# Revit family: efg_egg-20_60s(t)b2_60Hz
name_source: partatom
category: 機械設備
units: mm (PartAtom-declared; Revit-internal decimal feet)

## family parameters
OmniClass タイトル = Industrial Ventilating Equipment
OmniClass 番号 = 23.75.35.21.17
パーツ タイプ = 標準
ロード時にボイドで切り取り = はい
丸型コネクタ寸法 = 直径を使用
作業面ベース = いいえ
共有 = いいえ
常に垂直 = はい
部屋計算ポイント = いいえ

## types (8) — shared parameters
IfcExportAs = IfcFanType
IfcExportType = TUBEAXIAL
MID風量 = 0.0 m³/h
OmniClassCode = 23-33 31 19 11 17
URL = https://www.mitsubishielectric.co.jp
Uniclass2015Code = Pr_65_67_29_67
Uniclass2015Title = Propeller fans
Uniclass2015Version = Systems v1.9
ファンの種類 = 軸流羽根
仕様書バージョン = Version1.0
企業コード = 108420
分類コード = 50052503100110
周波数 = 60 Hz
呼称 = 有圧扇
法定耐用年数 = 15
製品リリース年月 = 2022年6月1日
製品出荷対象 = 国内
製造元 = 三菱電機株式会社
設置方法 = 壁付
説明 = 業務用有圧換気扇 店舗用 標準タイプ
負荷分類 = 3_ファン類
運転質量 = 0.00 kg

## per-type parameters (varying)
| type | D1 | D2 | Depth | H1 | Height | MAX風量 | MIN風量 | W1 | W2 | Width | 価格 | 極 | 極数 | 消費電力 | 相 | 羽根径 | 製品質量 | 質量 | 電動機出力 | 電圧 |
| EFG-20SB2 | 155  [stored 0.50853 ft] | 10  [stored 0.0328084 ft] | 195  [stored 0.639764 ft] | 244 | 322  [stored 1.05643 ft] | 660.0 m³/h | 490.0 m³/h | 244 | 210  [stored 0.688976 ft] | 322  [stored 1.05643 ft] | 57800 $ | 4 | 2 | 20 W | 1 | ∅200 | 5.00 kg | 6.00 kg | 15 W | 100 V |
| EFG-25SB2 | 155  [stored 0.50853 ft] | 20 | 205 | 294 | 372 | 1250.0 m³/h | 960.0 m³/h | 294 | 260 | 372 | 60900 $ | 4 | 2 | 40 W | 1 | ∅250 | 5.20 kg | 6.24 kg | 25 W | 100 V |
| EFG-30SB2 | 155  [stored 0.50853 ft] | 36 | 221 | 344 | 422 | 1940.0 m³/h | 1350.0 m³/h | 344 | 300 | 422 | 72300 $ | 4 | 2 | 59 W | 1 | ∅300 | 6.50 kg | 7.80 kg | 50 W | 100 V |
| EFG-35SB2 | 155  [stored 0.50853 ft] | 26 | 211 | 399 | 484 | 2740.0 m³/h | 2050.0 m³/h | 399 | 350 | 484 | 105000 $ | 4 | 2 | 108 W | 1 | ∅350 | 9.10 kg | 10.92 kg | 100 W | 100 V |
| EFG-40SB2 | 159 | 33 | 284 | 423 | 518 | 3700.0 m³/h | 2810.0 m³/h | 423 | 400 | 518 | 136000 $ | 4 | 2 | 172 W | 1 | ∅400 | 14.60 kg | 17.52 kg | 150 W | 100 V |
| EFG-40STB2 | 159 | 33 | 284 | 423 | 518 | 3750.0 m³/h | 0.0 m³/h | 423 | 400 | 518 | 133000 $ | 4 | 3 | 158 W | 3 | ∅400 | 14.30 kg | 17.16 kg | 150 W | 200 V |
| EGG-50STB2 | 189 | 55 | 350 | 524 | 620 | 6340.0 m³/h | 0.0 m³/h | 524 | 500 | 620 | 174000 $ | 6 | 3 | 305 W | 3 | ∅500 | 21.20 kg | 25.44 kg | 400 W | 200 V |
| EGG-60STB2 | 189 | 50  [stored 0.164042 ft] | 363 | 614 | 710 | 8900.0 m³/h | 0.0 m³/h | 614 | 600 | 710 | 233000 $ | 6 | 3 | 435 W | 3 | ∅600 | 25.90 kg | 31.08 kg | 400 W | 200 V |

note: column(s) folded — value = type name in every type: モデル

note: [stored X ft] marks values corroborated as IEEE doubles in the binary element streams (Revit-internal decimal feet)
